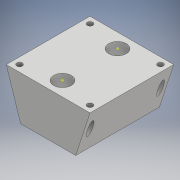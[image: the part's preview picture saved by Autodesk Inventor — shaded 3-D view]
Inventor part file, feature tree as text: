
AUTODESK INVENTOR PART (.ipt)
format: ipt  version: 2017 (Build 210142000, 142)  size: 140,288 bytes
history: native  units: mm
features: hole x3, sketch x3, extrude x2, other x2
ambient origin geometry x8: Origin, YZ Plane, XZ Plane, XY Plane, X Axis, Y Axis, Z Axis, Center Point
bodies: Solid1 (feature_tree)
feature tree (10):
  extrude  "Extrusion1"  Depth=38.0mm
  extrude  "Extrusion2"  Depth=4.2mm
  hole  "Hole1"  [1 undecoded]
  other  "Work Point1"
  other  "Work Point2"
  hole  "Hole2"  [1 undecoded]
  hole  "Hole3"  [1 undecoded]
  sketch  "Sketch1"  dims[d0=25.0mm d1=38.0mm]
  sketch  "Sketch2"  dims[d2=4.2mm d3=4.2mm]
  sketch  "Sketch3"  dims[d4=12.5mm d5=12.5mm d6=20.0mm d7=0.0mm d8=6.5mm d9=6.5mm d10=30.0mm d11=0.0mm d12=16.0mm d13=16.0mm d14=20.0mm d16=32.0mm d17=20.0mm d19=32.0mm d22=2.5mm d23=6.0mm d24=4.0mm d25=2.0mm d26=90.0deg d27=20.0mm d28=20.594885mm d49=10.0mm d50=10.0mm d31=8.0mm d32=6.0mm d33=4.0mm d34=2.0mm d35=90.0deg d36=16.0mm d37=20.594885mm d51=10.0mm d52=10.0mm d40=8.0mm d41=6.0mm d42=4.0mm d43=2.0mm d44=90.0deg d45=16.0mm d46=20.594885mm]
note: 3 required parameter values undecoded (feature->parameter linkage not recoverable at this tier; creation-order binding heuristic only, values carry confidence <= 0.55)
